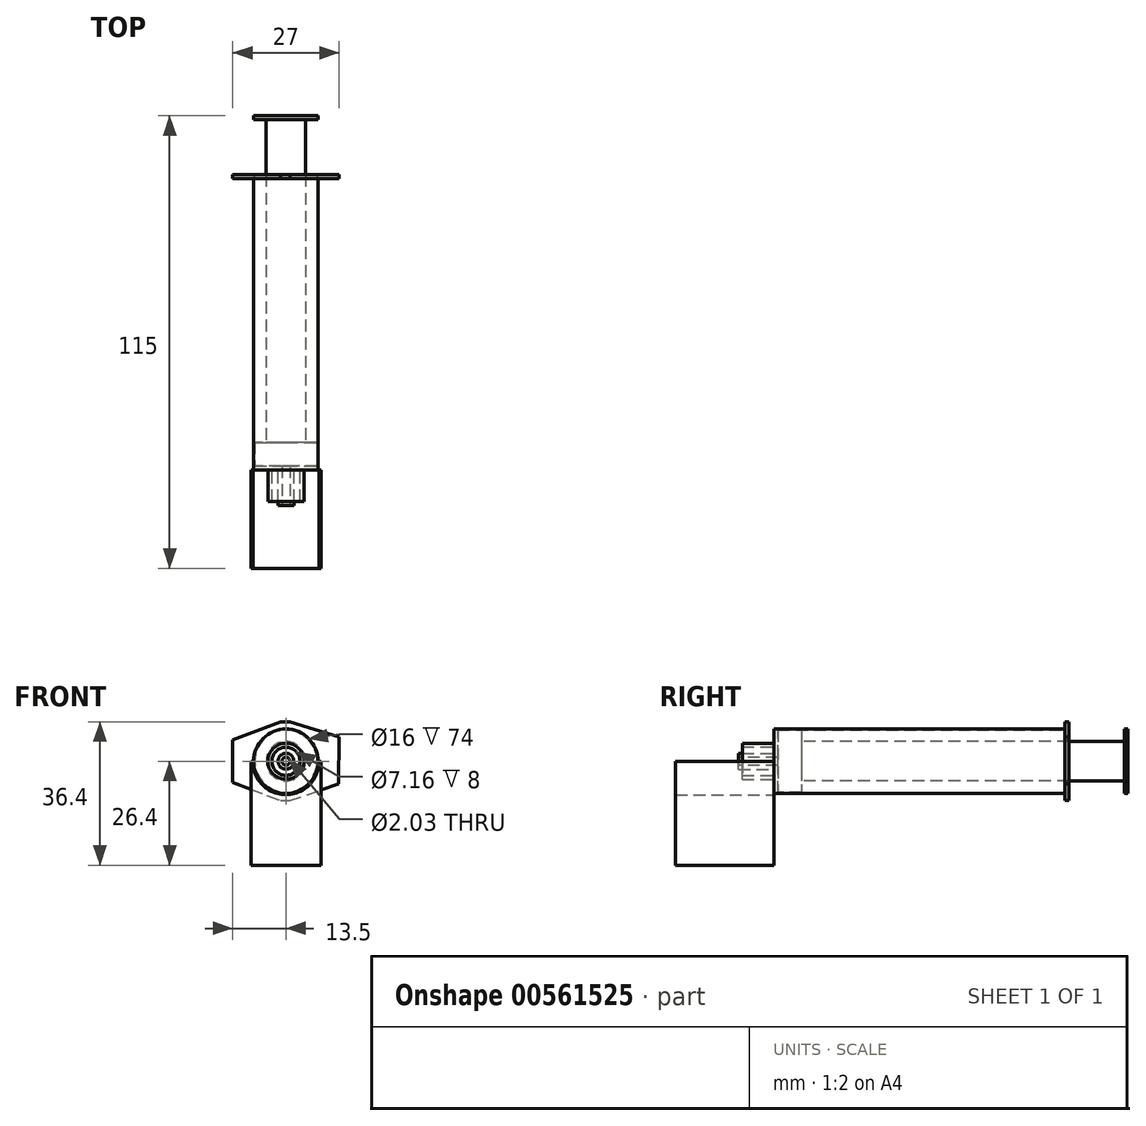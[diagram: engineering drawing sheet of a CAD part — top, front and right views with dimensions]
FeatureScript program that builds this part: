
annotation { "Feature Type Name" : "Feature", "Feature Type Description" : "" }
export const myFeature = defineFeature(function(context is Context, id is Id, definition is map)
    precondition{}
    {
        {
            var Q0;
            Q0=qCreatedBy(makeId("Front.planeOp"),FACE);
            var sketch = newSketch(context, id + "F0", { "sketchPlane" : qUnion([Q0])});
            skCircle(sketch, "E0", {"center": v(0, 0) * mm, "radius": 8.2 * mm});
            skSolve(sketch);
        }
        {
            var Q0;
            Q0=makeQuery(id+"F0.imprint","IMPRINT",FACE,{"disambiguationData":[TD([[makeQuery(id+"F0.imprint","IMPRINT",EDGE,{"derivedFrom":sQuery(id+"F0.wireOp",EDGE,"E0")}),1.0]])]});
            extrude(context, id + "F1", {"entities" : qUnion([Q0]), "depth" : 75 * mm, "offsetDistance" : 25 * mm});
        }
        {
            var Q0;
            Q0=qCreatedBy(makeId("Front.planeOp"),FACE);
            var sketch = newSketch(context, id + "F2", { "sketchPlane" : qUnion([Q0])});
            skPoint(sketch, "E1.middle", {"position": v(0, 0) * mm});
            skLineSegment(sketch, "E2", {"start": v(-13.5, 5.43) * mm, "end": v(-1.33, 10) * mm});
            skLineSegment(sketch, "E3", {"start": v(-1.33, 10) * mm, "end": v(1.06, 10) * mm});
            skLineSegment(sketch, "E4", {"start": v(1.06, 10) * mm, "end": v(13.5, 6.21) * mm});
            skLineSegment(sketch, "E5", {"start": v(-13.5, -5.43) * mm, "end": v(-1.33, -10) * mm});
            skLineSegment(sketch, "E6", {"start": v(-1.33, -10) * mm, "end": v(1.06, -10) * mm});
            skLineSegment(sketch, "E7", {"start": v(1.06, -10) * mm, "end": v(13.36, -5.79) * mm});
            skLineSegment(sketch, "E8", {"start": v(13.5, 6.21) * mm, "end": v(13.36, -5.79) * mm});
            skLineSegment(sketch, "E9", {"start": v(-13.5, 5.43) * mm, "end": v(-13.5, -5.43) * mm});
            skCircle(sketch, "E10", {"center": v(0, 0) * mm, "radius": 7.5 * mm});
            skSolve(sketch);
        }
        {
            var Q0;
            Q0=makeQuery(id+"F2.imprint","IMPRINT",FACE,{"disambiguationData":[TD([[makeQuery(id+"F2.imprint","IMPRINT",EDGE,{"derivedFrom":sQuery(id+"F2.wireOp",EDGE,"E2")}),-1.0]])]});
            extrude(context, id + "F3", {"entities" : qUnion([Q0]), "operationType" : NewBodyOperationType.ADD, "depth" : 1 * mm, "offsetDistance" : 25 * mm});
        }
        {
            var Q0;
            Q0=qCreatedBy(makeId("Front.planeOp"),FACE);
            var sketch = newSketch(context, id + "F4", { "sketchPlane" : qUnion([Q0])});
            skCircle(sketch, "E11", {"center": v(0, 0) * mm, "radius": 8 * mm});
            skSolve(sketch);
        }
        {
            var Q0;
            Q0=makeQuery(id+"F4.imprint","IMPRINT",FACE,{"disambiguationData":[TD([[makeQuery(id+"F4.imprint","IMPRINT",EDGE,{"derivedFrom":sQuery(id+"F4.wireOp",EDGE,"E11")}),1.0]])]});
            extrude(context, id + "F5", {"entities" : qUnion([Q0]), "operationType" : NewBodyOperationType.REMOVE, "depth" : 74 * mm, "offsetDistance" : 25 * mm});
        }
        {
            var Q0;
            Q0=makeQuery(id+"F1.opExtrude","CAP_FACE",FACE,{"disambiguationData":[OSD([sQuery(id+"F0.wireOp",EDGE,"E0")])],"isStart":false});
            var sketch = newSketch(context, id + "F6", { "sketchPlane" : qUnion([Q0])});
            skCircle(sketch, "E12", {"center": v(0, 0) * mm, "radius": 4.58 * mm});
            skCircle(sketch, "E13", {"center": v(0, 0) * mm, "radius": 3.58 * mm});
            skSolve(sketch);
        }
        {
            var Q0;
            Q0=makeQuery(id+"F6.imprint","IMPRINT",FACE,{"disambiguationData":[TD([[makeQuery(id+"F6.imprint","IMPRINT",EDGE,{"derivedFrom":sQuery(id+"F6.wireOp",EDGE,"E12")}),1.0]])]});
            extrude(context, id + "F7", {"entities" : qUnion([Q0]), "operationType" : NewBodyOperationType.ADD, "depth" : 8 * mm, "offsetDistance" : 25 * mm});
        }
        {
            var Q0;
            Q0=makeQuery(id+"F7.boolean.opBoolean","SPLIT",FACE,{"disambiguationData":[TD([makeQuery(id+"F7.opExtrude","SWEPT_FACE",FACE,{"disambiguationData":[OSD([sQuery(id+"F6.wireOp",EDGE,"E13")])]})])],"derivedFrom":makeQuery(id+"F1.opExtrude","CAP_FACE",FACE,{"disambiguationData":[OSD([sQuery(id+"F0.wireOp",EDGE,"E0")])],"isStart":false})});
            var sketch = newSketch(context, id + "F8", { "sketchPlane" : qUnion([Q0])});
            skCircle(sketch, "E14", {"center": v(0, 0) * mm, "radius": 2.02 * mm});
            skSolve(sketch);
        }
        {
            var Q0;
            Q0=qSketchRegion(id+"F8",true);
            extrude(context, id + "F9", {"entities" : qUnion([Q0]), "operationType" : NewBodyOperationType.ADD, "depth" : 9 * mm, "offsetDistance" : 25 * mm});
        }
        {
            var Q0;
            Q0=makeQuery(id+"F9.opExtrude","CAP_FACE",FACE,{"disambiguationData":[OSD([sQuery(id+"F8.wireOp",EDGE,"E14")])],"isStart":false});
            var sketch = newSketch(context, id + "F10", { "sketchPlane" : qUnion([Q0])});
            skCircle(sketch, "E15", {"center": v(0, 0) * mm, "radius": 1.01 * mm});
            skSolve(sketch);
        }
        {
            var Q0;
            Q0=qSketchRegion(id+"F10",true);
            extrude(context, id + "F11", {"entities" : qUnion([Q0]), "operationType" : NewBodyOperationType.REMOVE, "oppositeDirection" : true, "depth" : 75 * mm, "offsetDistance" : 25 * mm});
        }
        {
            var Q0;
            Q0=makeQuery(id+"F5.boolean.opBoolean","COPY",FACE,{"derivedFrom":makeQuery(id+"F5.opExtrude","CAP_FACE",FACE,{"disambiguationData":[OSD([sQuery(id+"F4.wireOp",EDGE,"E11")])],"isStart":false})});
            var sketch = newSketch(context, id + "F12", { "sketchPlane" : qUnion([Q0])});
            skCircle(sketch, "E16", {"center": v(0, 0) * mm, "radius": 7.9 * mm});
            skSolve(sketch);
        }
        {
            var Q0;
            Q0=qSketchRegion(id+"F12",true);
            extrude(context, id + "F13", {"entities" : qUnion([Q0]), "depth" : 6 * mm, "offsetDistance" : 25 * mm});
        }
        {
            var Q0;
            Q0=makeQuery(id+"F13.opExtrude","CAP_FACE",FACE,{"disambiguationData":[OSD([sQuery(id+"F12.wireOp",EDGE,"E16")])],"isStart":false});
            var sketch = newSketch(context, id + "F14", { "sketchPlane" : qUnion([Q0])});
            skCircle(sketch, "E17", {"center": v(0, 0) * mm, "radius": 5 * mm});
            skSolve(sketch);
        }
        {
            var Q0;
            Q0=qSketchRegion(id+"F14",true);
            extrude(context, id + "F15", {"entities" : qUnion([Q0]), "operationType" : NewBodyOperationType.ADD, "depth" : 82 * mm, "offsetDistance" : 25 * mm});
        }
        {
            var Q0;
            Q0=makeQuery(id+"F15.opExtrude","CAP_FACE",FACE,{"disambiguationData":[OSD([sQuery(id+"F14.wireOp",EDGE,"E17")])],"isStart":false});
            var sketch = newSketch(context, id + "F16", { "sketchPlane" : qUnion([Q0])});
            skCircle(sketch, "E18", {"center": v(0, 0) * mm, "radius": 8.2 * mm});
            skSolve(sketch);
        }
        {
            var Q0;
            Q0=qSketchRegion(id+"F16",true);
            extrude(context, id + "F17", {"entities" : qUnion([Q0]), "operationType" : NewBodyOperationType.ADD, "depth" : 1 * mm, "offsetDistance" : 25 * mm});
        }
        {
            var Q0;
            {var subQ0=sQuery(id+"F0.wireOp",EDGE,"E0");Q0=makeQuery(id+"F7.boolean.opBoolean","SPLIT",FACE,{"disambiguationData":[TD([makeQuery(id+"F1.opExtrude","SWEPT_FACE",FACE,{"disambiguationData":[OSD([subQ0])]})])],"derivedFrom":makeQuery(id+"F1.opExtrude","CAP_FACE",FACE,{"disambiguationData":[OSD([subQ0])],"isStart":false})});}
            var sketch = newSketch(context, id + "F18", { "sketchPlane" : qUnion([Q0])});
            skLineSegment(sketch, "E19", {"start": v(-8.2, 0) * mm, "end": v(-8.4, 0) * mm});
            skLineSegment(sketch, "E20", {"start": v(8.2, 0) * mm, "end": v(8.4, 0) * mm});
            skArc(sketch, "E21", {"start": v(-8.4, 0) * mm, "mid": v(0, -8.5) * mm, "end": v(8.4, 0) * mm});
            skLineSegment(sketch, "E22", {"start": v(8.4, 0) * mm, "end": v(8.9, 0) * mm});
            skLineSegment(sketch, "E23", {"start": v(-8.4, 0) * mm, "end": v(-8.9, 0) * mm});
            skLineSegment(sketch, "E24.top", {"start": v(-8.9, -26.4) * mm, "end": v(8.9, -26.4) * mm});
            skLineSegment(sketch, "E24.left", {"start": v(-8.9, 0) * mm, "end": v(-8.9, -26.4) * mm});
            skLineSegment(sketch, "E24.right", {"start": v(8.9, 0) * mm, "end": v(8.9, -26.4) * mm});
            skSolve(sketch);
        }
        {
            var Q0;
            Q0 = qSketchRegion(id + "F18", true);
            extrude(context, id + "F19", {"entities" : qUnion([Q0]), "depth" : 25 * mm, "offsetDistance" : 25 * mm});
        }
    });
